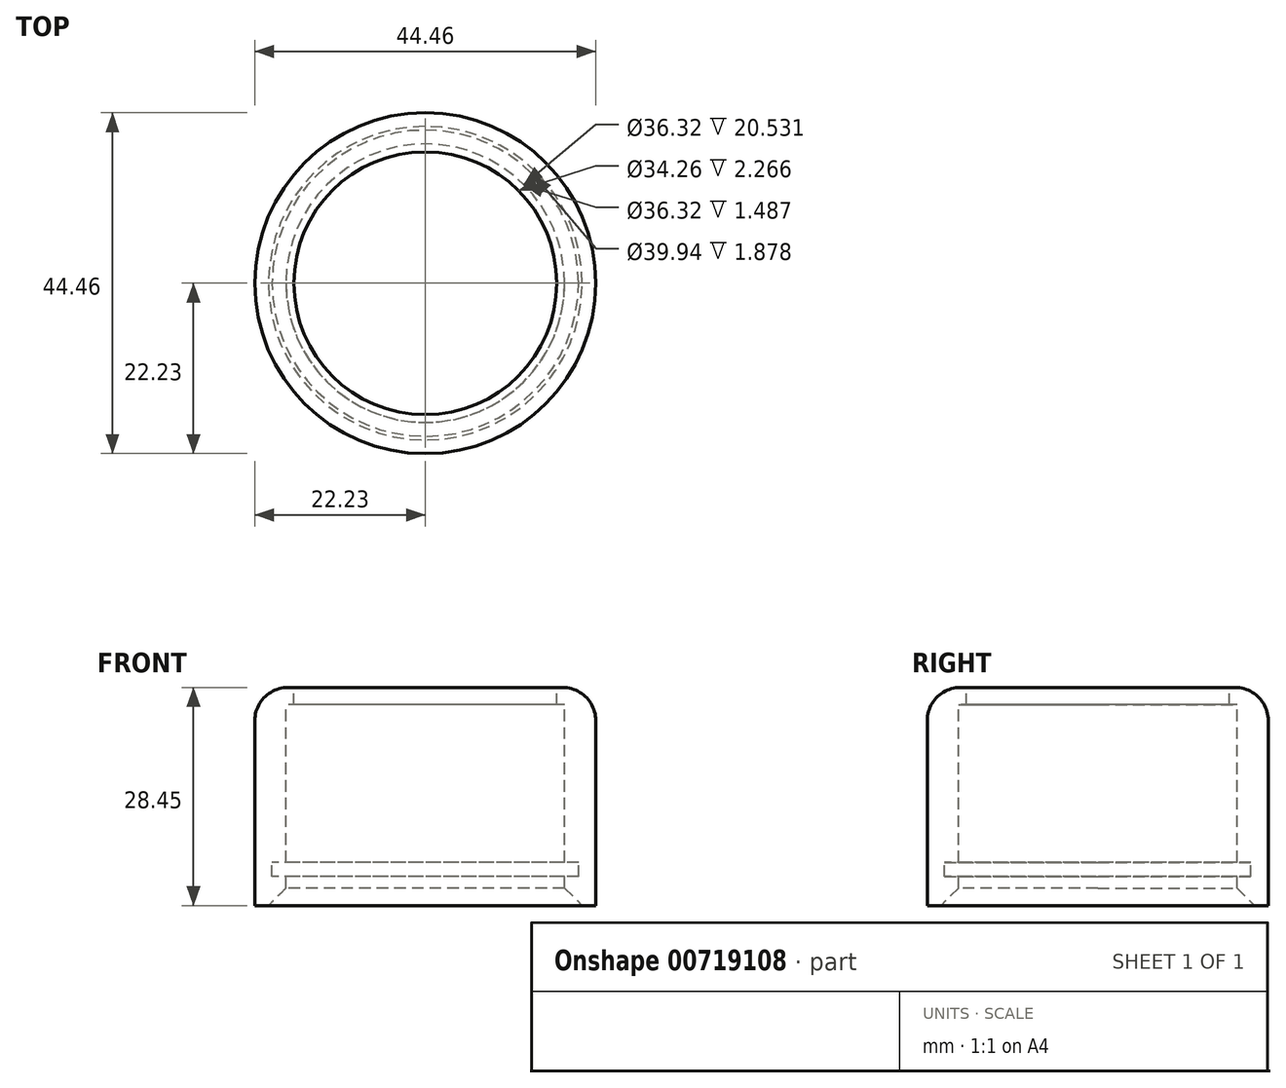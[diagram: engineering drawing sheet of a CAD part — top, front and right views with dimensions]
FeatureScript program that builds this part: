
annotation { "Feature Type Name" : "Feature", "Feature Type Description" : "" }
export const myFeature = defineFeature(function(context is Context, id is Id, definition is map)
    precondition{}
    {
        {
            var Q0;
            Q0=qCreatedBy(makeId("Front.planeOp"),FACE);
            var sketch = newSketch(context, id + "F0", { "sketchPlane" : qUnion([Q0])});
            skLineSegment(sketch, "E0", {"start": v(-22.23, 0) * mm, "end": v(-22.22, -28.45) * mm});
            skLineSegment(sketch, "E1", {"start": v(-22.22, -28.45) * mm, "end": v(-18.16, -28.45) * mm});
            skLineSegment(sketch, "E2", {"start": v(-18.16, -28.45) * mm, "end": v(-18.16, -24.68) * mm});
            skLineSegment(sketch, "E3", {"start": v(-19.97, -24.68) * mm, "end": v(-18.16, -24.68) * mm});
            skLineSegment(sketch, "E4", {"start": v(-18.16, -22.8) * mm, "end": v(-18.16, -2.27) * mm});
            skLineSegment(sketch, "E5", {"start": v(-18.16, -2.27) * mm, "end": v(-17.13, -2.27) * mm});
            skLineSegment(sketch, "E6", {"start": v(-17.13, -2.27) * mm, "end": v(-17.13, 0) * mm});
            skLineSegment(sketch, "E7", {"start": v(-17.13, 0) * mm, "end": v(-22.23, 0) * mm});
            skLineSegment(sketch, "E8", {"start": v(0, 0) * mm, "end": v(0, -28.45) * mm});
            skLineSegment(sketch, "E9", {"start": v(-18.16, -24.68) * mm, "end": v(-18.16, -24.68) * mm});
            skLineSegment(sketch, "E10", {"start": v(-19.97, -24.68) * mm, "end": v(-19.97, -22.8) * mm});
            skLineSegment(sketch, "E11", {"start": v(-19.97, -22.8) * mm, "end": v(-18.16, -22.8) * mm});
            skSolve(sketch);
        }
        {
            var Q0;
            Q0 = qSketchRegion(id + "F0", true);
            var Q1;
            Q1=sQuery(id+"F0.wireOp",EDGE,"E8");
            revolve(context, id + "F1", {"surfaceOperationType" : NewSurfaceOperationType.NEW, "entities" : qUnion([Q0]), "axis" : qUnion([Q1]), "revolveType" : RevolveType.FULL});
        }
        {
            var Q0;
            Q0=makeQuery(id+"F1.opRevolve","SWEPT_EDGE",EDGE,{"disambiguationData":[OSD([sQuery(id+"F0.wireOp",EDGE,"E1"),sQuery(id+"F0.wireOp",EDGE,"E2")])]});
            chamfer(context, id + "F2", {"entities" : qUnion([Q0]), "width" : 2.3 * mm, "tangentPropagation" : true});
        }
        {
            var Q0;
            Q0=makeQuery(id+"F1.opRevolve","SWEPT_EDGE",EDGE,{"disambiguationData":[OSD([sQuery(id+"F0.wireOp",EDGE,"E0"),sQuery(id+"F0.wireOp",EDGE,"E7")])]});
            fillet(context, id + "F3", {"entities" : qUnion([Q0]), "radius" : 4.32 * mm, "tangentPropagation" : true, "allowEdgeOverflow" : false});
        }
    });
